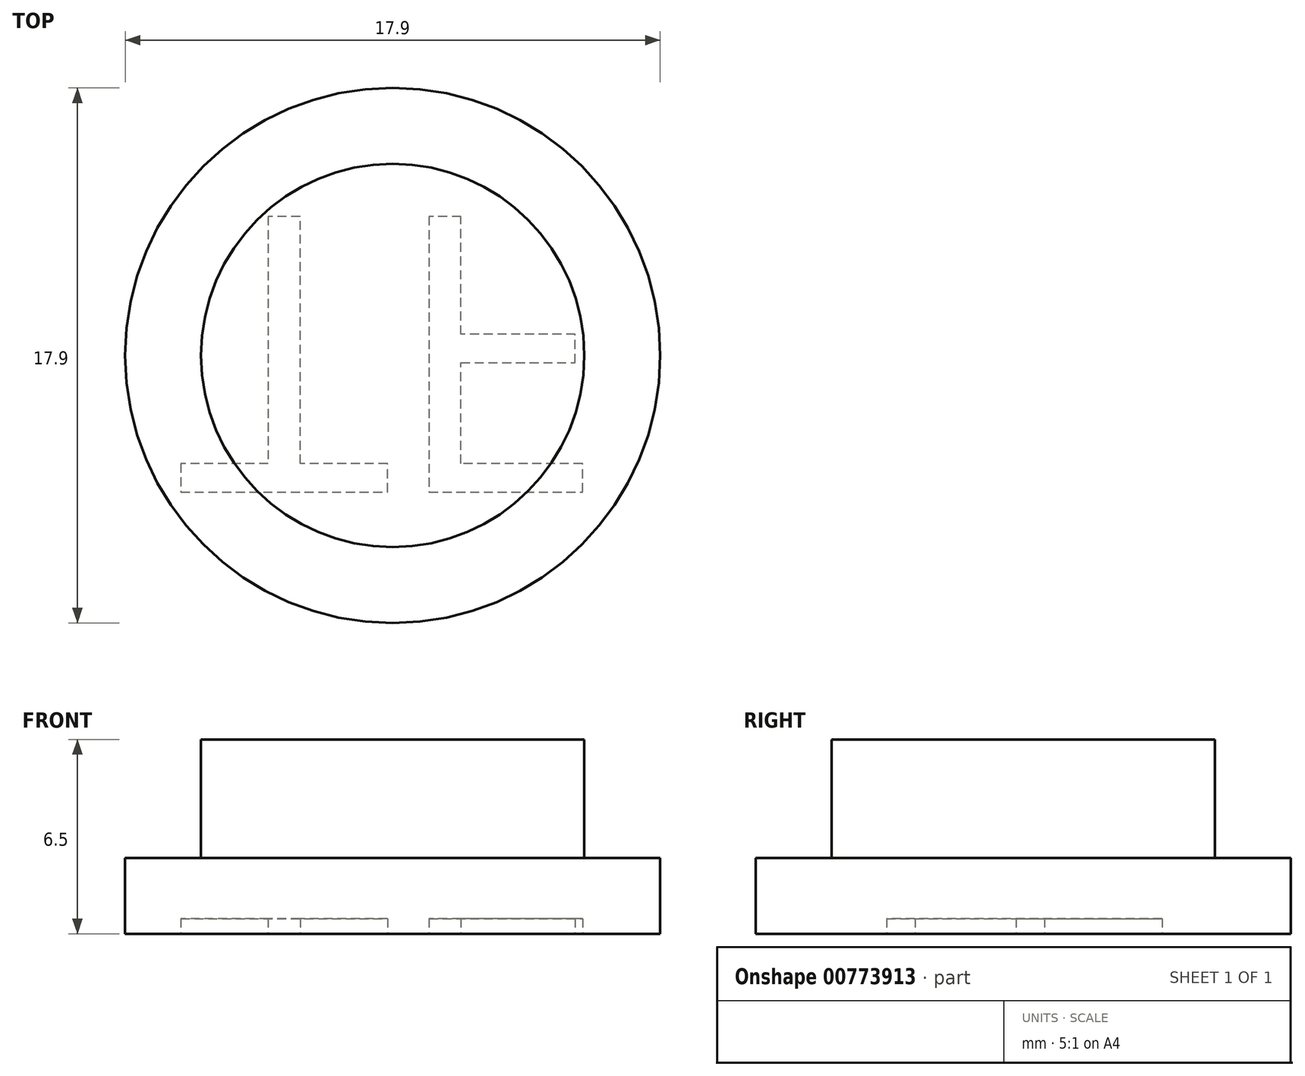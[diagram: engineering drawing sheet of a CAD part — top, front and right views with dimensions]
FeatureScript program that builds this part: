
annotation { "Feature Type Name" : "Feature", "Feature Type Description" : "" }
export const myFeature = defineFeature(function(context is Context, id is Id, definition is map)
    precondition{}
    {
        {
            var Q0;
            Q0=qCreatedBy(makeId("Front.planeOp"),FACE);
            var sketch = newSketch(context, id + "F0", { "sketchPlane" : qUnion([Q0])});
            skLineSegment(sketch, "E0", {"start": v(0, 0) * mm, "end": v(0, 8.02) * mm, "construction": true});
            skLineSegment(sketch, "E1", {"start": v(0, 0) * mm, "end": v(-8.95, 0) * mm});
            skLineSegment(sketch, "E2", {"start": v(-8.95, 0) * mm, "end": v(-8.95, 2.54) * mm});
            skLineSegment(sketch, "E3", {"start": v(-8.95, 2.54) * mm, "end": v(-6.41, 2.54) * mm});
            skLineSegment(sketch, "E4", {"start": v(-6.41, 2.54) * mm, "end": v(-6.41, 6.5) * mm});
            skLineSegment(sketch, "E5", {"start": v(-6.41, 6.5) * mm, "end": v(0, 6.5) * mm});
            skLineSegment(sketch, "E6", {"start": v(0, 6.5) * mm, "end": v(0, 0) * mm});
            skSolve(sketch);
        }
        {
            var Q0;
            Q0=qSketchRegion(id+"F0",true);
            var Q1;
            Q1=sQuery(id+"F0.wireOp",EDGE,"E0");
            revolve(context, id + "F1", {"surfaceOperationType" : NewSurfaceOperationType.NEW, "entities" : qUnion([Q0]), "axis" : qUnion([Q1]), "revolveType" : RevolveType.FULL});
        }
        {
            var Q0;
            Q0=makeQuery(id+"F1.opRevolve","SWEPT_FACE",FACE,{"disambiguationData":[OSD([sQuery(id+"F0.wireOp",EDGE,"E1")])]});
            var sketch = newSketch(context, id + "F2", { "sketchPlane" : qUnion([Q0])});
            skText(sketch, "E7", { "text": "TF", "fontName": "OpenSans-Regular.ttf"});
            const initialGuessF2  = {"E7": [-0.0072, -0.00465, 1, 0, 0.0093]};
            skSetInitialGuess(sketch, initialGuessF2);
            skSolve(sketch);
        }
        {
            var Q0;
            Q0=qSketchRegion(id+"F2",true);
            extrude(context, id + "F3", {"entities" : qUnion([Q0]), "operationType" : NewBodyOperationType.REMOVE, "oppositeDirection" : true, "depth" : 0.5 * mm, "offsetDistance" : 25.4 * mm});
        }
    });
